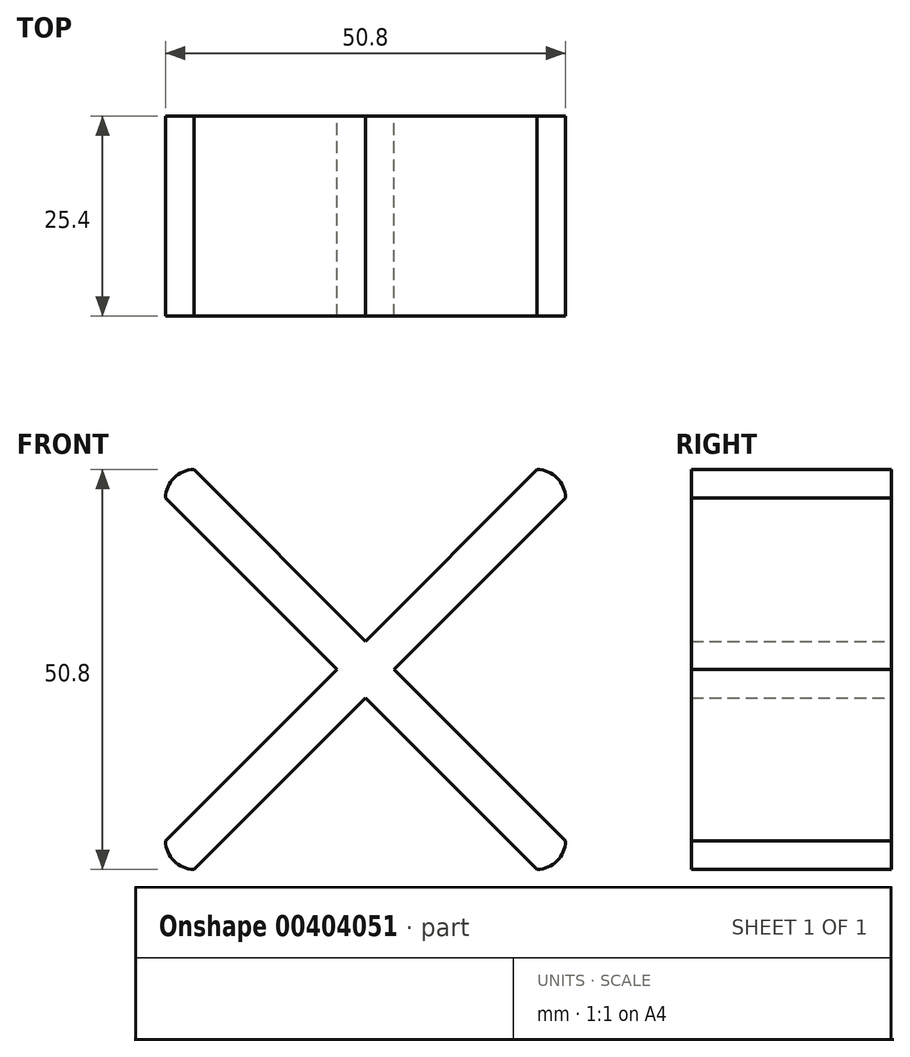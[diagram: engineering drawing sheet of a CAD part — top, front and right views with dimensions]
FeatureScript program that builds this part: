
annotation { "Feature Type Name" : "Feature", "Feature Type Description" : "" }
export const myFeature = defineFeature(function(context is Context, id is Id, definition is map)
    precondition{}
    {
        {
            var Q0;
            Q0=qCreatedBy(makeId("Front.planeOp"),FACE);
            var sketch = newSketch(context, id + "F0", { "sketchPlane" : qUnion([Q0])});
            skLineSegment(sketch, "E0.bottom", {"start": v(-21.72, 25.4) * mm, "end": v(21.72, 25.4) * mm});
            skLineSegment(sketch, "E0.top", {"start": v(-21.72, -25.4) * mm, "end": v(21.72, -25.4) * mm});
            skLineSegment(sketch, "E0.left", {"start": v(-25.4, 21.72) * mm, "end": v(-25.4, -21.72) * mm});
            skLineSegment(sketch, "E0.right", {"start": v(25.4, 21.72) * mm, "end": v(25.4, -21.72) * mm});
            skPoint(sketch, "E0.middle", {"position": v(0, 0) * mm});
            skLineSegment(sketch, "E1", {"start": v(-25.4, 25.4) * mm, "end": v(25.4, -25.4) * mm});
            skLineSegment(sketch, "E2", {"start": v(25.4, 25.4) * mm, "end": v(-25.4, -25.4) * mm});
            skLineSegment(sketch, "E3", {"start": v(-25.4, 21.8) * mm, "end": v(21.8, -25.4) * mm});
            skLineSegment(sketch, "E4", {"start": v(-21.8, 25.4) * mm, "end": v(25.4, -21.8) * mm});
            skLineSegment(sketch, "E5", {"start": v(-25.4, -21.8) * mm, "end": v(21.8, 25.4) * mm});
            skLineSegment(sketch, "E6", {"start": v(-21.8, -25.4) * mm, "end": v(25.4, 21.8) * mm});
            skPoint(sketch, "E7.visualSharp", {"position": v(-25.4, 25.4) * mm});
            skArc(sketch, "E7.filletArc", {"start": v(-21.72, 25.4) * mm, "mid": v(-24.32, 24.32) * mm, "end": v(-25.4, 21.72) * mm});
            skPoint(sketch, "E8.visualSharp", {"position": v(25.4, 25.4) * mm});
            skArc(sketch, "E8.filletArc", {"start": v(25.4, 21.72) * mm, "mid": v(24.32, 24.32) * mm, "end": v(21.72, 25.4) * mm});
            skPoint(sketch, "E9.visualSharp", {"position": v(-25.4, -25.4) * mm});
            skArc(sketch, "E9.filletArc", {"start": v(-25.4, -21.72) * mm, "mid": v(-24.32, -24.32) * mm, "end": v(-21.72, -25.4) * mm});
            skPoint(sketch, "E10.visualSharp", {"position": v(25.4, -25.4) * mm});
            skArc(sketch, "E10.filletArc", {"start": v(21.72, -25.4) * mm, "mid": v(24.32, -24.32) * mm, "end": v(25.4, -21.72) * mm});
            skSolve(sketch);
        }
        {
            var Q0;
            {var subQ0=sQuery(id+"F0.wireOp",EDGE,"E7.filletArc");var subQ1=sQuery(id+"F0.wireOp",EDGE,"E1");var subQ2=makeQuery(id+"F0.imprint","INTERSECT",VERTEX,{"derivedFrom":[subQ1,subQ0]});Q0=makeQuery(id+"F0.imprint","IMPRINT",FACE,{"disambiguationData":[TD([[makeQuery(id+"F0.imprint","IMPRINT",EDGE,{"disambiguationData":[TD([[subQ2,-1.0]])],"derivedFrom":subQ1}),-1.0]])]});}
            var Q1;
            {var subQ0=sQuery(id+"F0.wireOp",EDGE,"E7.filletArc");var subQ1=sQuery(id+"F0.wireOp",EDGE,"E1");var subQ2=makeQuery(id+"F0.imprint","INTERSECT",VERTEX,{"derivedFrom":[subQ1,subQ0]});Q1=makeQuery(id+"F0.imprint","IMPRINT",FACE,{"disambiguationData":[TD([[makeQuery(id+"F0.imprint","IMPRINT",EDGE,{"disambiguationData":[TD([[subQ2,-1.0]])],"derivedFrom":subQ1}),1.0]])]});}
            var Q2;
            {var subQ0=sQuery(id+"F0.wireOp",EDGE,"E5");var subQ1=sQuery(id+"F0.wireOp",EDGE,"E1");var subQ2=makeQuery(id+"F0.imprint","INTERSECT",VERTEX,{"derivedFrom":[subQ1,subQ0]});Q2=makeQuery(id+"F0.imprint","IMPRINT",FACE,{"disambiguationData":[TD([[makeQuery(id+"F0.imprint","IMPRINT",EDGE,{"disambiguationData":[TD([[subQ2,-1.0]])],"derivedFrom":subQ1}),-1.0]])]});}
            var Q3;
            {var subQ0=sQuery(id+"F0.wireOp",EDGE,"E5");var subQ1=sQuery(id+"F0.wireOp",EDGE,"E1");var subQ2=makeQuery(id+"F0.imprint","INTERSECT",VERTEX,{"derivedFrom":[subQ1,subQ0]});Q3=makeQuery(id+"F0.imprint","IMPRINT",FACE,{"disambiguationData":[TD([[makeQuery(id+"F0.imprint","IMPRINT",EDGE,{"disambiguationData":[TD([[subQ2,-1.0]])],"derivedFrom":subQ1}),1.0]])]});}
            var Q4;
            {var subQ0=sQuery(id+"F0.wireOp",EDGE,"E2");var subQ1=sQuery(id+"F0.wireOp",EDGE,"E1");var subQ2=makeQuery(id+"F0.imprint","INTERSECT",VERTEX,{"derivedFrom":[subQ1,subQ0]});Q4=makeQuery(id+"F0.imprint","IMPRINT",FACE,{"disambiguationData":[TD([[makeQuery(id+"F0.imprint","IMPRINT",EDGE,{"disambiguationData":[TD([[subQ2,-1.0]])],"derivedFrom":subQ1}),1.0]])]});}
            var Q5;
            {var subQ0=sQuery(id+"F0.wireOp",EDGE,"E2");var subQ1=sQuery(id+"F0.wireOp",EDGE,"E1");var subQ2=makeQuery(id+"F0.imprint","INTERSECT",VERTEX,{"derivedFrom":[subQ1,subQ0]});Q5=makeQuery(id+"F0.imprint","IMPRINT",FACE,{"disambiguationData":[TD([[makeQuery(id+"F0.imprint","IMPRINT",EDGE,{"disambiguationData":[TD([[subQ2,-1.0]])],"derivedFrom":subQ1}),-1.0]])]});}
            var Q6;
            {var subQ0=sQuery(id+"F0.wireOp",EDGE,"E8.filletArc");var subQ1=sQuery(id+"F0.wireOp",EDGE,"E2");var subQ2=makeQuery(id+"F0.imprint","INTERSECT",VERTEX,{"derivedFrom":[subQ1,subQ0]});Q6=makeQuery(id+"F0.imprint","IMPRINT",FACE,{"disambiguationData":[TD([[makeQuery(id+"F0.imprint","IMPRINT",EDGE,{"disambiguationData":[TD([[subQ2,-1.0]])],"derivedFrom":subQ1}),-1.0]])]});}
            var Q7;
            {var subQ0=sQuery(id+"F0.wireOp",EDGE,"E8.filletArc");var subQ1=sQuery(id+"F0.wireOp",EDGE,"E2");var subQ2=makeQuery(id+"F0.imprint","INTERSECT",VERTEX,{"derivedFrom":[subQ1,subQ0]});Q7=makeQuery(id+"F0.imprint","IMPRINT",FACE,{"disambiguationData":[TD([[makeQuery(id+"F0.imprint","IMPRINT",EDGE,{"disambiguationData":[TD([[subQ2,-1.0]])],"derivedFrom":subQ1}),1.0]])]});}
            var Q8;
            {var subQ0=sQuery(id+"F0.wireOp",EDGE,"E10.filletArc");var subQ1=sQuery(id+"F0.wireOp",EDGE,"E1");var subQ2=makeQuery(id+"F0.imprint","INTERSECT",VERTEX,{"derivedFrom":[subQ1,subQ0]});Q8=makeQuery(id+"F0.imprint","IMPRINT",FACE,{"disambiguationData":[TD([[makeQuery(id+"F0.imprint","IMPRINT",EDGE,{"disambiguationData":[TD([[subQ2,1.0]])],"derivedFrom":subQ1}),1.0]])]});}
            var Q9;
            {var subQ0=sQuery(id+"F0.wireOp",EDGE,"E9.filletArc");var subQ1=sQuery(id+"F0.wireOp",EDGE,"E2");var subQ2=makeQuery(id+"F0.imprint","INTERSECT",VERTEX,{"derivedFrom":[subQ1,subQ0]});Q9=makeQuery(id+"F0.imprint","IMPRINT",FACE,{"disambiguationData":[TD([[makeQuery(id+"F0.imprint","IMPRINT",EDGE,{"disambiguationData":[TD([[subQ2,1.0]])],"derivedFrom":subQ1}),-1.0]])]});}
            var Q10;
            {var subQ0=sQuery(id+"F0.wireOp",EDGE,"E9.filletArc");var subQ1=sQuery(id+"F0.wireOp",EDGE,"E2");var subQ2=makeQuery(id+"F0.imprint","INTERSECT",VERTEX,{"derivedFrom":[subQ1,subQ0]});Q10=makeQuery(id+"F0.imprint","IMPRINT",FACE,{"disambiguationData":[TD([[makeQuery(id+"F0.imprint","IMPRINT",EDGE,{"disambiguationData":[TD([[subQ2,1.0]])],"derivedFrom":subQ1}),1.0]])]});}
            var Q11;
            {var subQ0=sQuery(id+"F0.wireOp",EDGE,"E10.filletArc");var subQ1=sQuery(id+"F0.wireOp",EDGE,"E1");var subQ2=makeQuery(id+"F0.imprint","INTERSECT",VERTEX,{"derivedFrom":[subQ1,subQ0]});Q11=makeQuery(id+"F0.imprint","IMPRINT",FACE,{"disambiguationData":[TD([[makeQuery(id+"F0.imprint","IMPRINT",EDGE,{"disambiguationData":[TD([[subQ2,1.0]])],"derivedFrom":subQ1}),-1.0]])]});}
            extrude(context, id + "F1", {"entities" : qUnion([Q0, Q1, Q2, Q3, Q4, Q5, Q6, Q7, Q8, Q9, Q10, Q11]), "depth" : 25.4 * mm});
        }
    });
